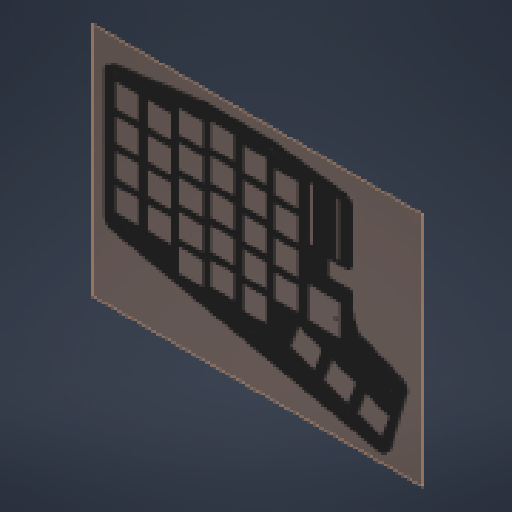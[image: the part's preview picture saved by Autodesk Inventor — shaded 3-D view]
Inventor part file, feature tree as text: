
AUTODESK INVENTOR PART (.ipt)
format: ipt  version: 2024.3 (Build 283343000, 343)  size: 541,696 bytes
history: native  units: in
note: dims shown in document units (in); Inventor stores cm internally (conversion verified against a paired STEP export)
features: other x3, plane x1, extrude x1, fillet x1, sketch x1, reference x1
ambient origin geometry x8: Origin, YZ Plane, XZ Plane, XY Plane, X Axis, Y Axis, Z Axis, Center Point
bodies: Solid1 (feature_tree)
feature tree (8):
  plane  "Work Plane1"
  extrude  "Extrusion1"  Depth=0.57in
  fillet  "Fillet1"  Radius=0.57in
  sketch  "Sketch1"  dims[d2=0.57in d3=0.57in d4=0.57in d5=0.57in d6=0.57in d7=0.57in d8=0.57in d9=0.57in d10=0.57in d11=0.57in d12=0.57in d13=0.57in d14=0.57in d15=0.57in d16=0.57in d17=0.57in d18=0.57in d19=0.57in d20=0.57in d21=0.57in d22=0.57in d23=0.57in d24=0.57in d25=0.57in d26=0.57in d27=0.57in d28=0.57in d29=0.57in d30=0.57in d31=0.57in d32=0.57in d33=0.57in d34=0.57in d35=0.57in d36=0.57in d37=0.57in d38=0.57in d39=0.57in d40=0.57in d41=0.57in d42=0.57in d43=0.57in d44=0.57in d45=0.57in d46=0.57in d47=0.57in d48=0.57in d49=0.57in d50=0.57in d51=0.57in d52=0.57in d53=0.57in d54=0.57in d55=0.57in d56=0.285in d57=0.57in d58=0.57in d59=0.285in d60=0.57in d61=0.57in d62=0.57in d63=0.57in d64=0.57in d65=0.57in d66=0.57in d67=0.57in d68=0.285in d69=0.285in d70=0.285in d71=0.285in d72=0.285in d73=0.285in d74=0.285in d75=0.285in d76=90.0deg d77=0.75in d78=0.75in d79=0.0625in d80=0.125in d81=0.0625in d82=0.0625in d83=0.125in d84=0.0625in d85=0.0625in d86=0.0625in d87=0.0in d88=0.0625in d91=0.0625in d92=0.0625in d93=0.0625in]
  reference  "Reference1"
  other  "<userpath>\Documents\GitHub\clackenPersonal\Case Cad\Main Case Assembly.iam"
  other  "Main Case Assembly.iam"
  other  "Split V2:1"
